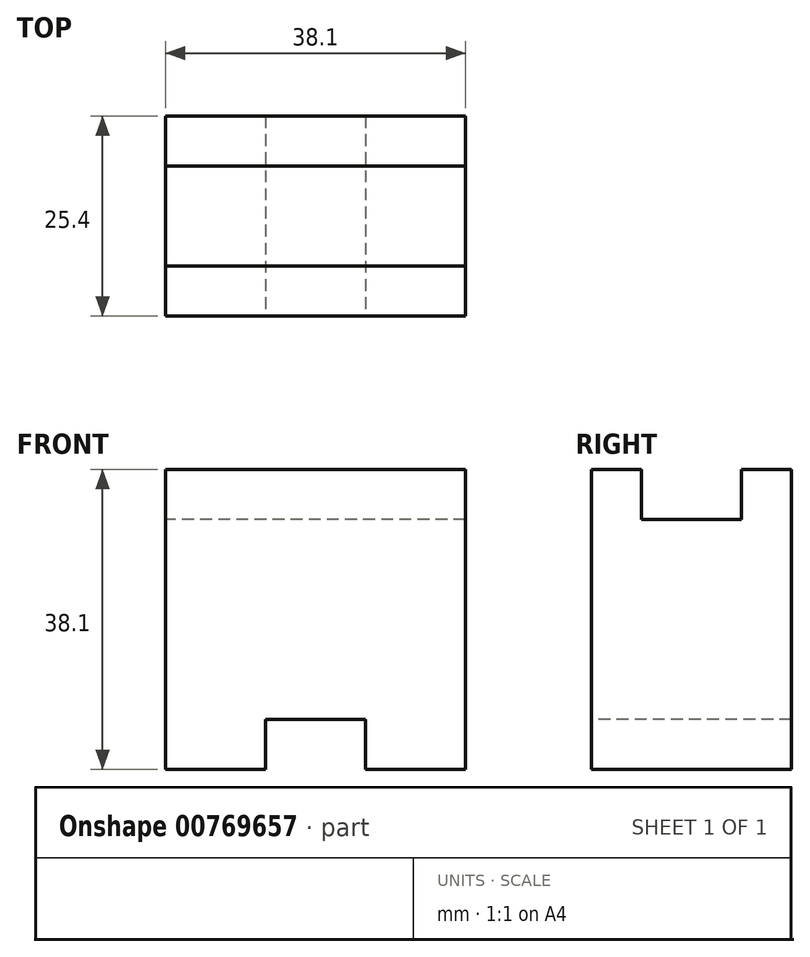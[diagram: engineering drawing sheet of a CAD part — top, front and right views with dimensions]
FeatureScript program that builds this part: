
annotation { "Feature Type Name" : "Feature", "Feature Type Description" : "" }
export const myFeature = defineFeature(function(context is Context, id is Id, definition is map)
    precondition{}
    {
        {
            var Q0;
            Q0=qCreatedBy(makeId("Right.planeOp"),FACE);
            var sketch = newSketch(context, id + "F0", { "sketchPlane" : qUnion([Q0])});
            skLineSegment(sketch, "E0", {"start": v(0, 0) * mm, "end": v(25.4, 0) * mm});
            skLineSegment(sketch, "E1", {"start": v(25.4, 0) * mm, "end": v(25.4, 38.1) * mm});
            skLineSegment(sketch, "E2", {"start": v(25.4, 38.1) * mm, "end": v(0, 38.1) * mm});
            skLineSegment(sketch, "E3", {"start": v(0, 38.1) * mm, "end": v(0, 0) * mm});
            skLineSegment(sketch, "E4", {"start": v(25.4, 38.1) * mm, "end": v(19.05, 38.1) * mm});
            skLineSegment(sketch, "E5", {"start": v(0, 38.1) * mm, "end": v(6.35, 38.1) * mm});
            skLineSegment(sketch, "E6", {"start": v(6.35, 38.1) * mm, "end": v(6.35, 31.75) * mm});
            skLineSegment(sketch, "E7", {"start": v(6.35, 31.75) * mm, "end": v(19.05, 31.75) * mm});
            skLineSegment(sketch, "E8", {"start": v(19.05, 31.75) * mm, "end": v(19.05, 38.1) * mm});
            skSolve(sketch);
        }
        {
            var Q0;
            {var subQ3=sQuery(id+"F0.wireOp",EDGE,"E6");var subQ6=makeQuery(id+"F0.imprint","IMPRINT",EDGE,{"derivedFrom":subQ3});Q0=qUnion([makeQuery(id+"F0.imprint","IMPRINT",FACE,{"disambiguationData":[TD([[makeQuery(id+"F0.imprint","IMPRINT",EDGE,{"derivedFrom":sQuery(id+"F0.wireOp",EDGE,"E0")}),1.0]])]}),makeQuery(id+"F0.imprint","IMPRINT",FACE,{"disambiguationData":[TD([[subQ6,1.0]])]})]);}
            extrude(context, id + "F1", {"entities" : qUnion([Q0]), "depth" : 38.1 * mm, "offsetDistance" : 25.4 * mm});
        }
        {
            var Q0;
            {var subQ2=sQuery(id+"F0.wireOp",EDGE,"E6");Q0=makeQuery(id+"F0.imprint","IMPRINT",FACE,{"disambiguationData":[TD([[makeQuery(id+"F0.imprint","IMPRINT",EDGE,{"derivedFrom":subQ2}),1.0]])]});}
            extrude(context, id + "F2", {"entities" : qUnion([Q0]), "operationType" : NewBodyOperationType.REMOVE, "oppositeDirection" : true, "depth" : -38.1 * mm, "offsetDistance" : 25.4 * mm});
        }
        {
            var Q0;
            Q0=makeQuery(id+"F1.opExtrude","SWEPT_FACE",FACE,{"disambiguationData":[OSD([sQuery(id+"F0.wireOp",EDGE,"E3")])]});
            var sketch = newSketch(context, id + "F3", { "sketchPlane" : qUnion([Q0])});
            skLineSegment(sketch, "E9", {"start": v(38.1, 0) * mm, "end": v(25.4, 0) * mm});
            skLineSegment(sketch, "E10", {"start": v(25.4, 0) * mm, "end": v(25.4, 6.35) * mm});
            skLineSegment(sketch, "E11", {"start": v(25.4, 6.35) * mm, "end": v(12.7, 6.35) * mm});
            skLineSegment(sketch, "E12", {"start": v(12.7, 6.35) * mm, "end": v(12.7, 0) * mm});
            skLineSegment(sketch, "E13", {"start": v(12.7, 0) * mm, "end": v(0, 0) * mm});
            skSolve(sketch);
        }
        {
            var Q0;
            Q0 = qSketchRegion(id + "F3", true);
            var Q1;
            {var subQ0=sQuery(id+"F3.wireOp",EDGE,"E10");Q1=makeQuery(id+"F3.imprint","IMPRINT",FACE,{"disambiguationData":[TD([[makeQuery(id+"F3.imprint","IMPRINT",EDGE,{"derivedFrom":subQ0}),1.0]])]});}
            extrude(context, id + "F4", {"entities" : qUnion([Q0, Q1]), "operationType" : NewBodyOperationType.REMOVE, "oppositeDirection" : true, "depth" : 25.4 * mm, "offsetDistance" : 25.4 * mm});
        }
    });
